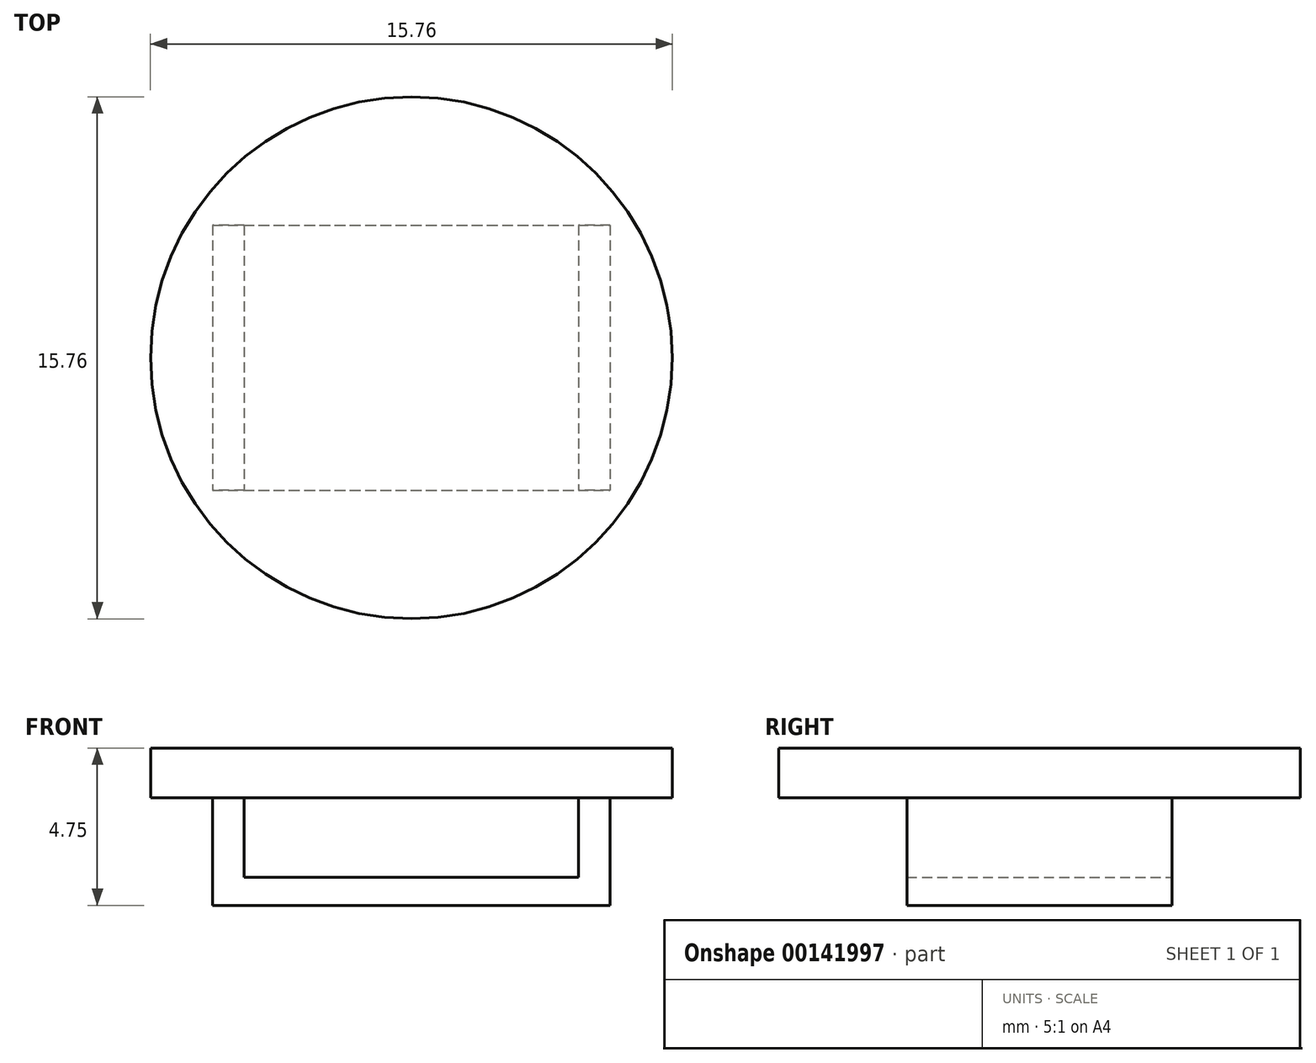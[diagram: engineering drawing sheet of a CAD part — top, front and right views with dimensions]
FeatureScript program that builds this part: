
annotation { "Feature Type Name" : "Feature", "Feature Type Description" : "" }
export const myFeature = defineFeature(function(context is Context, id is Id, definition is map)
    precondition{}
    {
        {
            var Q0;
            Q0=qCreatedBy(makeId("Front.planeOp"),FACE);
            var sketch = newSketch(context, id + "F0", { "sketchPlane" : qUnion([Q0])});
            skLineSegment(sketch, "E0.bottom", {"start": v(-6, 0) * mm, "end": v(6, 0) * mm});
            skLineSegment(sketch, "E0.top", {"start": v(-6, -4) * mm, "end": v(6, -4) * mm});
            skLineSegment(sketch, "E0.left", {"start": v(-6, 0) * mm, "end": v(-6, -4) * mm});
            skLineSegment(sketch, "E0.right", {"start": v(6, 0) * mm, "end": v(6, -4) * mm});
            skLineSegment(sketch, "E1.bottom", {"start": v(-5.05, -0.7) * mm, "end": v(5.05, -0.7) * mm});
            skLineSegment(sketch, "E1.top", {"start": v(-5.05, -3.15) * mm, "end": v(5.05, -3.15) * mm});
            skLineSegment(sketch, "E1.left", {"start": v(-5.05, -0.7) * mm, "end": v(-5.05, -3.15) * mm});
            skLineSegment(sketch, "E1.right", {"start": v(5.05, -0.7) * mm, "end": v(5.05, -3.15) * mm});
            skSolve(sketch);
        }
        {
            var Q0;
            Q0=makeQuery(id+"F0.imprint","IMPRINT",FACE,{"disambiguationData":[TD([[makeQuery(id+"F0.imprint","IMPRINT",EDGE,{"derivedFrom":sQuery(id+"F0.wireOp",EDGE,"E0.bottom")}),-1.0]])]});
            extrude(context, id + "F1", {"entities" : qUnion([Q0]), "endBound" : BoundingType.SYMMETRIC, "depth" : 8 * mm});
        }
        {
            var Q0;
            Q0=qCreatedBy(makeId("Top.planeOp"),FACE);
            var sketch = newSketch(context, id + "F2", { "sketchPlane" : qUnion([Q0])});
            skCircle(sketch, "E2", {"center": v(0, 0) * mm, "radius": 7.88 * mm});
            skSolve(sketch);
        }
        {
            var Q0;
            Q0 = qSketchRegion(id + "F2", true);
            extrude(context, id + "F3", {"entities" : qUnion([Q0]), "operationType" : NewBodyOperationType.ADD, "endBound" : BoundingType.SYMMETRIC, "depth" : 1.5 * mm});
        }
    });
